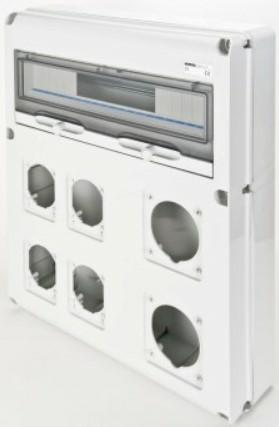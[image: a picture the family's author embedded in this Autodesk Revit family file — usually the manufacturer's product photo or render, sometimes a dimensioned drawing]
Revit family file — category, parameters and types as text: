
# Revit family: Building-QuadriIEC309-GEWISS-68QDIN-QUADRI-PRESE-20MOD_6PRESE
name_source: partatom
category: Apparecchi elettrici
units: mm (PartAtom-declared; Revit-internal decimal feet)

## family parameters
Condiviso = No
Host = Superficie
Mantenere orientamento annotazione = Sì
Punto di calcolo locali = Sì
Quota connettore circolare = Usa diametro
Taglio con vuoti quando caricato = No
Tipo di parte = Normale

## types (1)
- GW68021N - Q-DIN 20M 2PR.63A 4PR.16/32A IP65
    Catalogo = BUILDING
    Catalogo Serie = 68 QDIN
    Classe isolamento = II
    Codice EAN = 8011564744882
    Codice Electrocod = 2242
    Colore = Grigio RAL 7035
    Conformità normativa = EN 60208 - EN 60670-1 - IEC 60670-24
    Descrizione = Q-DIN 20M 2PR.63A 4PR.16/32A IP65
    Glow Wire Test = 650°C
    Grado di protezione = IP65
    IDF = 4c8860f2-720f-44d2-a6f5-9eaa74ffdce7
    IDT = c4e5c53f-a295-41ab-9992-af314b14205a
    Immagine tipo = GW68021N.jpg
    L_Moduli = 380 mm  [stored 1.24672 ft]
    Modello = GW68021N
    N. coperchi ciechi in dotazione = 2 IEC 309 16/32 A+1 63 A
    N. mod. EN 50022 = 20
    N. prese alloggiabili = 2 IEC 309 63 A - 4 IEC 309 16/32 A
    N_Moduli = 20 mm  [stored 0.0656168 ft]
    POMELLO = bianco
    PRESA = rosso
    Potenza dissipabile A (W) = 30
    Potenza dissipabile B (W) = 92
    Produttore = GEWISS S.p.A.
    Prospetto di default = 1219 mm
    Resistenza agli urti = IK08
    SEO = Quadretto
    STRUTTURA = RAL - 7035
    STRUTTURA ALTA = Poche
    Scheda Tecnica = https://www.gewiss.com
    Spostamento_S = 1000 mm  [stored 3.28084 ft]
    Temperatura di utilizzo = -25 +40 °C
    Termopressione con biglia = 70 °C
    Tipo versione = Vuoto
    Tipologia di installazione = Da parete
    URL = https://www.gewiss.com
    VETRO = Vetro
    Versione file RFA = 21.5

note: [stored X ft] marks values corroborated as IEEE doubles in the binary element streams (Revit-internal decimal feet)

## geometry (parser evidence)
native form markers: Sweep x5
no freeform markers — native parametric forms only
